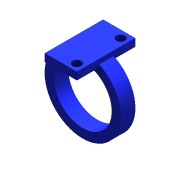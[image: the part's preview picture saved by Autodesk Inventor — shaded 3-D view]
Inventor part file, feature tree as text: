
AUTODESK INVENTOR PART (.ipt)
format: ipt  version: 2016 (Build 200138000, 138)  size: 114,176 bytes
history: native  units: mm
features: sketch x5, extrude x2, plane x1, hole x1
ambient origin geometry x8: Origin, YZ Plane, XZ Plane, XY Plane, X Axis, Y Axis, Z Axis, Center Point
bodies: Solid1 (feature_tree)
feature tree (9):
  extrude  "Extrusion1"  Depth=20.0mm
  sketch  "Sketch3"  dims[d9=5.0mm d10=0.0mm d11=12.0mm]
  plane  "Work Plane1"
  sketch  "Sketch4"  dims[d12=2.5mm d13=0.0mm d16=11.0mm]
  extrude  "Extrusion2"  Depth=5.0mm
  hole  "Hole1"  [1 undecoded]
  sketch  "Sketch2"  dims[d7=20.0mm d8=26.0mm]
  sketch  "Sketch5"  dims[d17=7.5mm]
  sketch  "Sketch6"  dims[d18=12.5mm d19=5.5mm d20=2.5mm d21=2.5mm d22=2.5mm d23=2.85mm d24=6.0mm d25=4.0mm d26=2.0mm d27=90.0deg d28=8.0mm d29=20.594885mm d30=2.5mm]
note: 1 required parameter value undecoded (feature->parameter linkage not recoverable at this tier; creation-order binding heuristic only, values carry confidence <= 0.55)
